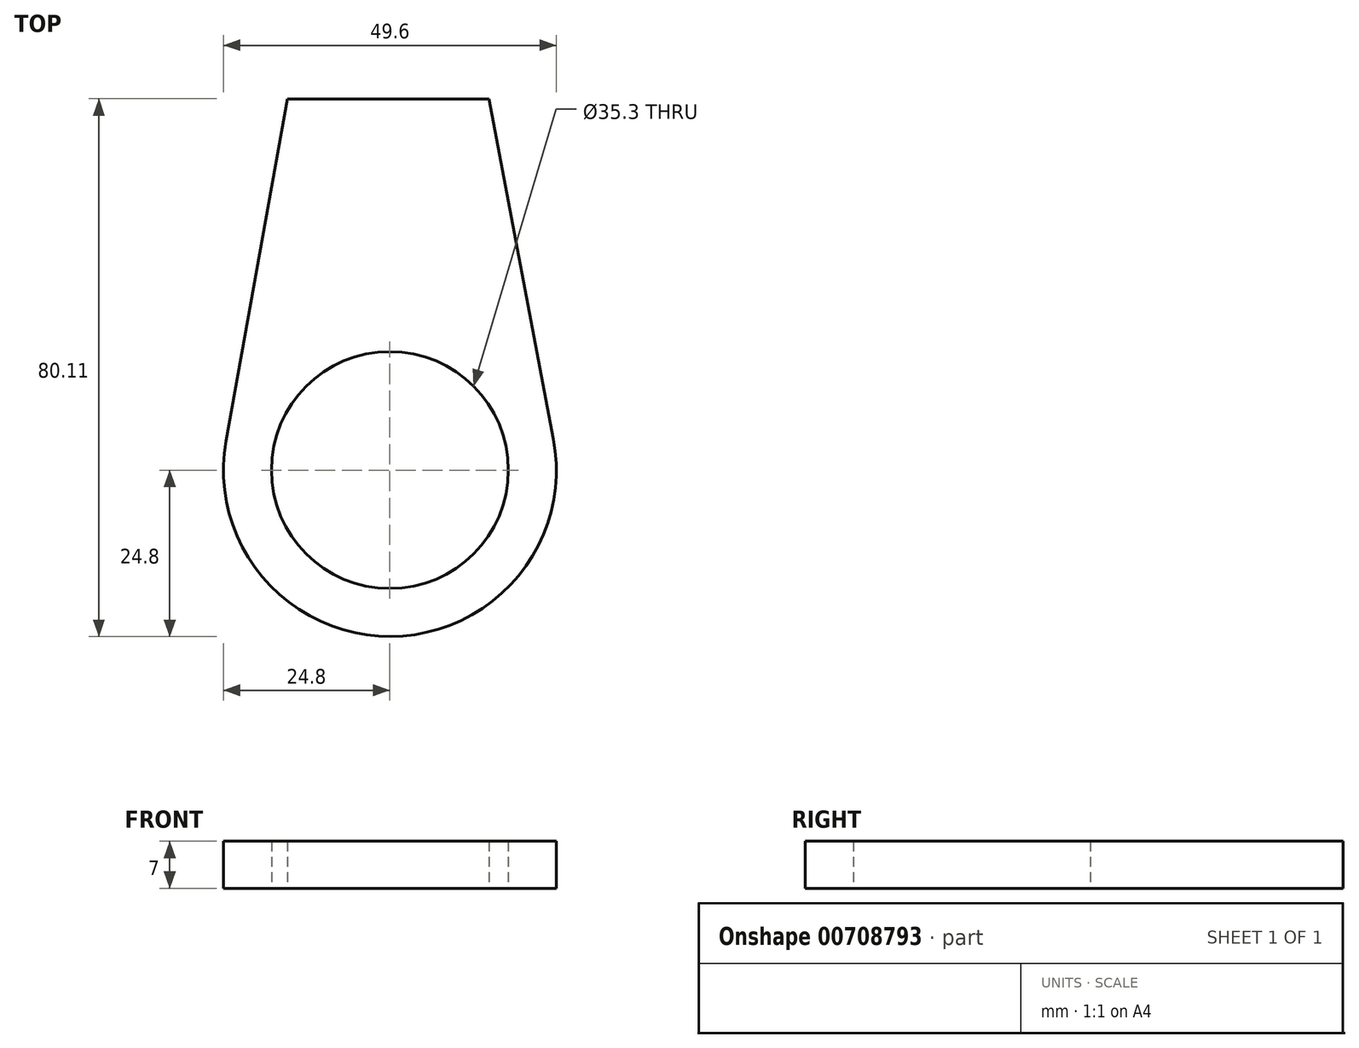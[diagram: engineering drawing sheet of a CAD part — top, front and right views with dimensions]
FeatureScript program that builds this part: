
annotation { "Feature Type Name" : "Feature", "Feature Type Description" : "" }
export const myFeature = defineFeature(function(context is Context, id is Id, definition is map)
    precondition{}
    {
        {
            var Q0;
            Q0=qCreatedBy(makeId("Top.planeOp"),FACE);
            var sketch = newSketch(context, id + "F0", { "sketchPlane" : qUnion([Q0])});
            skCircle(sketch, "E0", {"center": v(0, 0) * mm, "radius": 24.8 * mm});
            skCircle(sketch, "E1", {"center": v(0, 0) * mm, "radius": 17.65 * mm});
            skLineSegment(sketch, "E2", {"start": v(-15.3, 55.3) * mm, "end": v(14.74, 55.3) * mm});
            skLineSegment(sketch, "E3", {"start": v(-15.3, 55.3) * mm, "end": v(-25.2, 0) * mm});
            skLineSegment(sketch, "E4", {"start": v(14.74, 55.3) * mm, "end": v(25.24, 0) * mm});
            skSolve(sketch);
        }
        {
            var Q0;
            Q0 = qSketchRegion(id + "F0", true);
            extrude(context, id + "F1", {"entities" : qUnion([Q0]), "depth" : 7 * mm, "offsetDistance" : 25 * mm});
        }
    });
